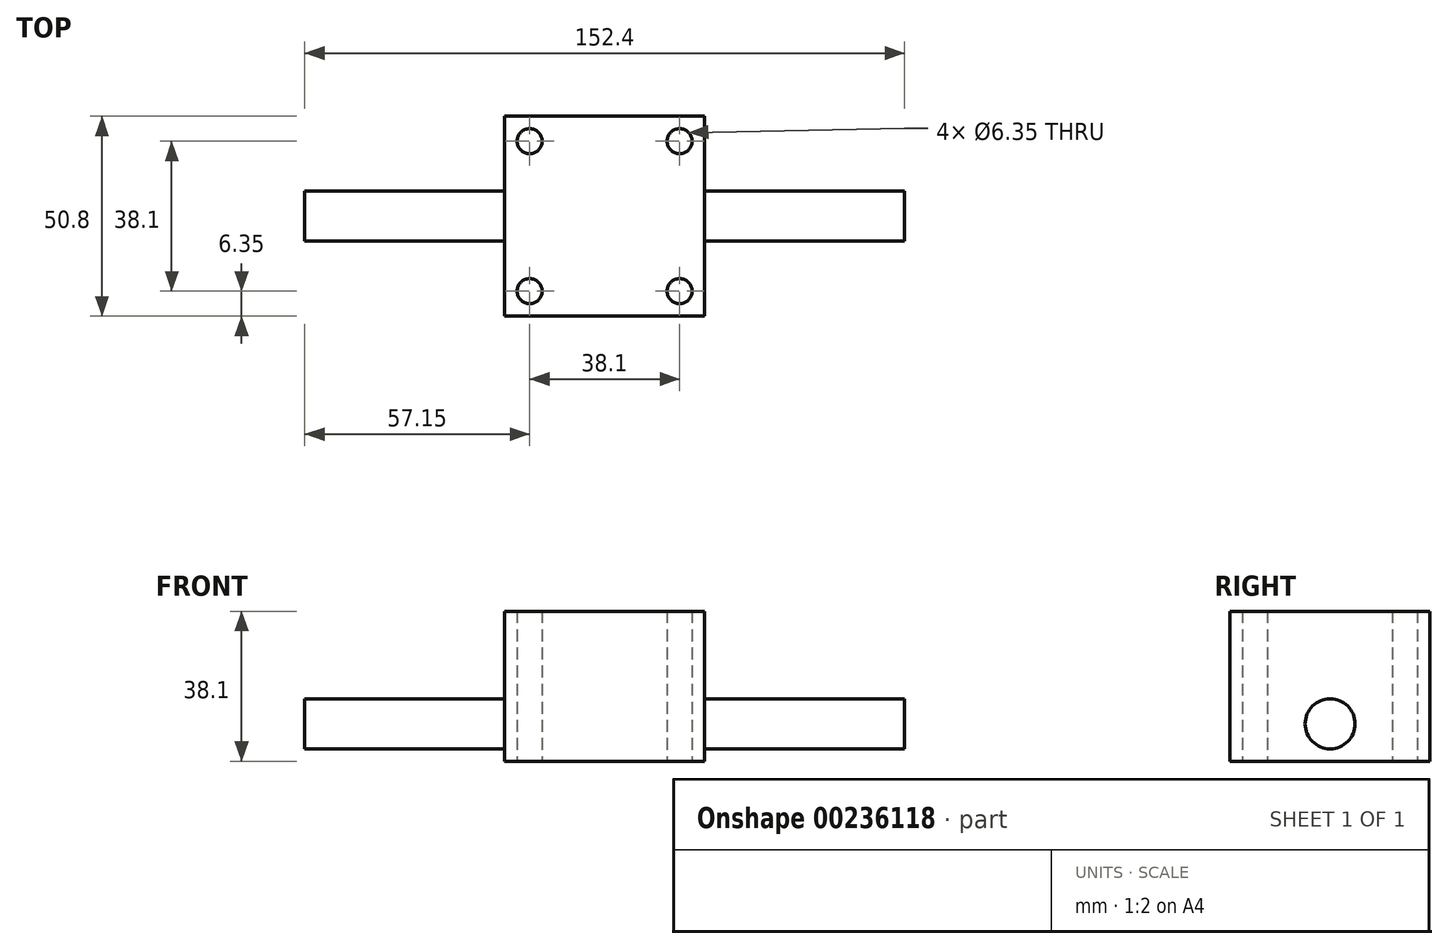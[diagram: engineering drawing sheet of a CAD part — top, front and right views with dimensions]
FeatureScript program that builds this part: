
annotation { "Feature Type Name" : "Feature", "Feature Type Description" : "" }
export const myFeature = defineFeature(function(context is Context, id is Id, definition is map)
    precondition{}
    {
        {
            var Q0;
            Q0=qCreatedBy(makeId("Top.planeOp"),FACE);
            var sketch = newSketch(context, id + "F0", { "sketchPlane" : qUnion([Q0])});
            skLineSegment(sketch, "E0.bottom", {"start": v(25.4, 25.4) * mm, "end": v(-25.4, 25.4) * mm});
            skLineSegment(sketch, "E0.top", {"start": v(25.4, -25.4) * mm, "end": v(-25.4, -25.4) * mm});
            skLineSegment(sketch, "E0.left", {"start": v(25.4, 25.4) * mm, "end": v(25.4, -25.4) * mm});
            skLineSegment(sketch, "E0.right", {"start": v(-25.4, 25.4) * mm, "end": v(-25.4, -25.4) * mm});
            skPoint(sketch, "E0.middle", {"position": v(0, 0) * mm});
            skCircle(sketch, "E1", {"center": v(-19.05, 19.05) * mm, "radius": 3.18 * mm});
            skCircle(sketch, "E2.MirrorC", {"center": v(19.05, 19.05) * mm, "radius": 3.18 * mm});
            skCircle(sketch, "E3.MirrorC", {"center": v(-19.05, -19.05) * mm, "radius": 3.18 * mm});
            skCircle(sketch, "E4.MirrorC", {"center": v(19.05, -19.05) * mm, "radius": 3.18 * mm});
            skSolve(sketch);
        }
        {
            var Q0;
            Q0=makeQuery(id+"F0.imprint","IMPRINT",FACE,{"disambiguationData":[TD([[makeQuery(id+"F0.imprint","IMPRINT",EDGE,{"derivedFrom":sQuery(id+"F0.wireOp",EDGE,"E0.bottom")}),1.0]])]});
            extrude(context, id + "F1", {"entities" : qUnion([Q0]), "endBound" : BoundingType.SYMMETRIC, "depth" : 38.1 * mm});
        }
        {
            var Q0;
            Q0=qCreatedBy(makeId("Right.planeOp"),FACE);
            var sketch = newSketch(context, id + "F2", { "sketchPlane" : qUnion([Q0])});
            skCircle(sketch, "E5", {"center": v(0, -9.53) * mm, "radius": 6.35 * mm});
            skSolve(sketch);
        }
        {
            var Q0;
            Q0 = qSketchRegion(id + "F2", true);
            extrude(context, id + "F3", {"entities" : qUnion([Q0]), "operationType" : NewBodyOperationType.ADD, "endBound" : BoundingType.SYMMETRIC, "depth" : 152.4 * mm});
        }
    });
